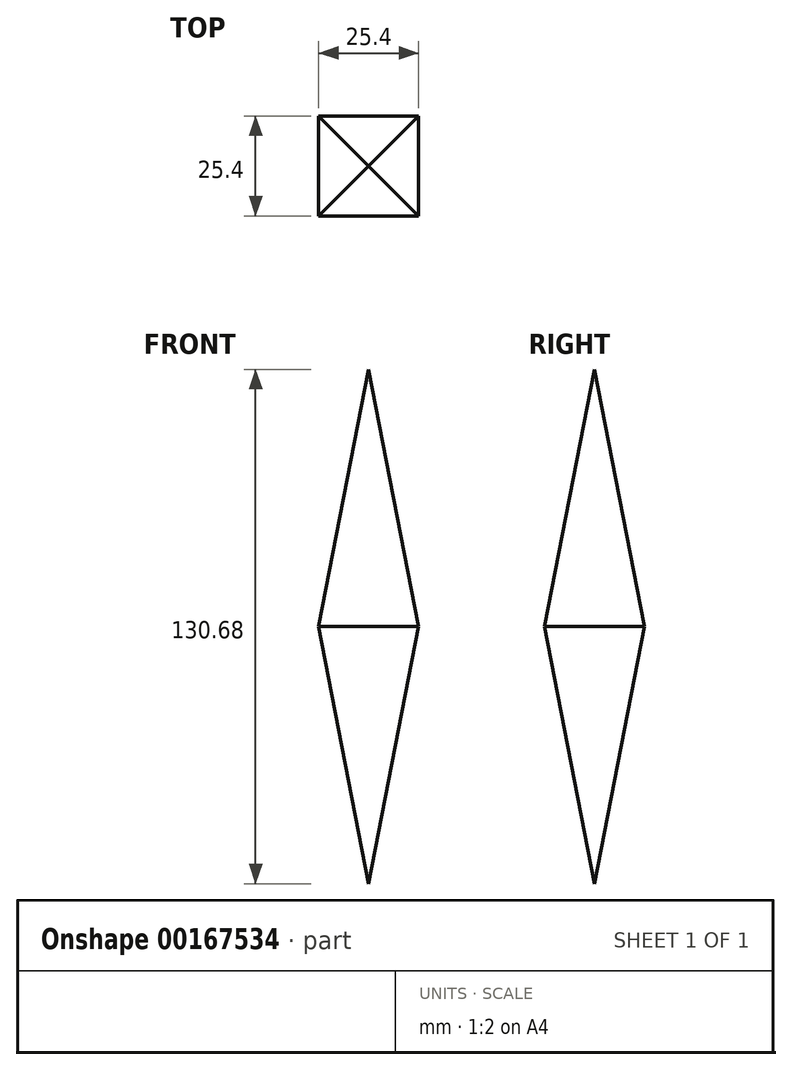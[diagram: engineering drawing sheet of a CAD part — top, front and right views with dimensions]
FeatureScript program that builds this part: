
annotation { "Feature Type Name" : "Feature", "Feature Type Description" : "" }
export const myFeature = defineFeature(function(context is Context, id is Id, definition is map)
    precondition{}
    {
        {
            var Q0;
            Q0=qCreatedBy(makeId("Top.planeOp"),FACE);
            var sketch = newSketch(context, id + "F0", { "sketchPlane" : qUnion([Q0])});
            skLineSegment(sketch, "E0.bottom", {"start": v(12.7, -12.7) * mm, "end": v(-12.7, -12.7) * mm});
            skLineSegment(sketch, "E0.top", {"start": v(12.7, 12.7) * mm, "end": v(-12.7, 12.7) * mm});
            skLineSegment(sketch, "E0.left", {"start": v(12.7, -12.7) * mm, "end": v(12.7, 12.7) * mm});
            skLineSegment(sketch, "E0.right", {"start": v(-12.7, -12.7) * mm, "end": v(-12.7, 12.7) * mm});
            skPoint(sketch, "E0.middle", {"position": v(0, 0) * mm});
            skSolve(sketch);
        }
        {
            var Q0;
            Q0 = qSketchRegion(id + "F0", true);
            var Q1;
            Q1=makeQuery(id+"F0.imprint","IMPRINT",FACE,{"disambiguationData":[TD([[makeQuery(id+"F0.imprint","IMPRINT",EDGE,{"derivedFrom":sQuery(id+"F0.wireOp",EDGE,"E0.bottom")}),-1.0]])]});
            extrude(context, id + "F1", {"entities" : qUnion([Q0, Q1]), "depth" : 73.66 * mm, "hasDraft" : true, "draftAngle" : 11 * degree, "draftPullDirection" : true, "hasSecondDirection" : true, "secondDirectionOppositeDirection" : true, "secondDirectionDepth" : 90.68 * mm, "hasSecondDirectionDraft" : true, "secondDirectionDraftAngle" : 11 * degree, "secondDirectionDraftPullDirection" : true});
        }
    });
